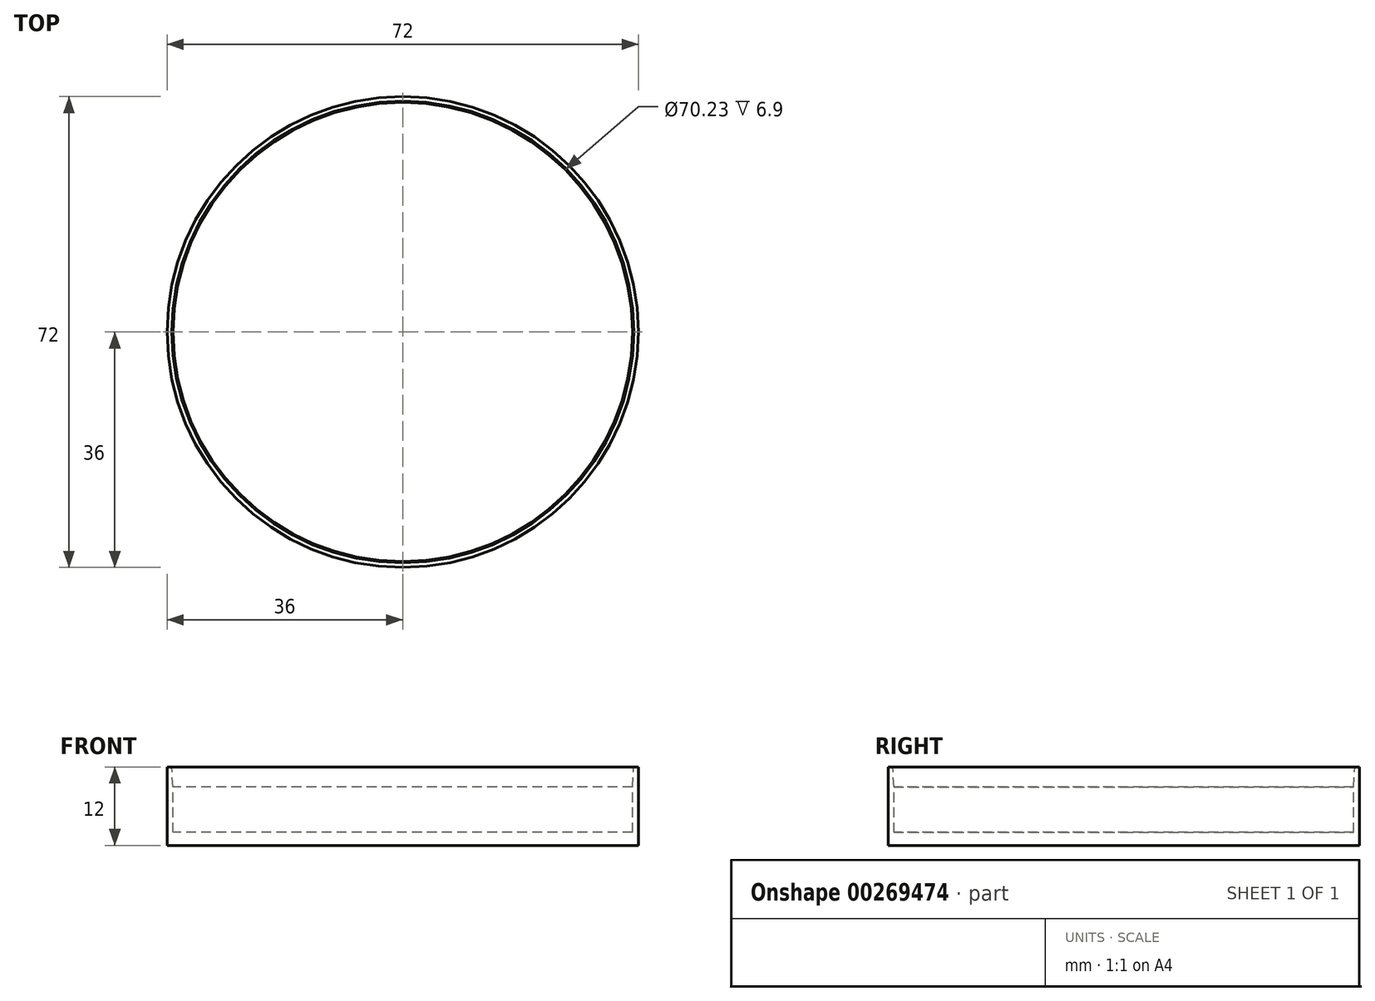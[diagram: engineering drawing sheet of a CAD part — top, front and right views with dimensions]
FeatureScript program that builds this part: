
annotation { "Feature Type Name" : "Feature", "Feature Type Description" : "" }
export const myFeature = defineFeature(function(context is Context, id is Id, definition is map)
    precondition{}
    {
        {
            var Q0;
            Q0=qCreatedBy(makeId("Top.planeOp"),FACE);
            var sketch = newSketch(context, id + "F0", { "sketchPlane" : qUnion([Q0])});
            skCircle(sketch, "E0", {"center": v(0, 0) * mm, "radius": 36 * mm});
            skSolve(sketch);
        }
        {
            var Q0;
            Q0=makeQuery(id+"F0.imprint","IMPRINT",FACE,{"disambiguationData":[TD([[makeQuery(id+"F0.imprint","IMPRINT",EDGE,{"derivedFrom":sQuery(id+"F0.wireOp",EDGE,"E0")}),1.0]])]});
            var Q1;
            Q1 = qSketchRegion(id + "F0", true);
            extrude(context, id + "F1", {"entities" : qUnion([Q0, Q1]), "depth" : 12 * mm});
        }
        {
            var Q0;
            Q0=makeQuery(id+"F1.opExtrude","CAP_FACE",FACE,{"disambiguationData":[OSD([sQuery(id+"F0.wireOp",EDGE,"E0")])],"isStart":false});
            var sketch = newSketch(context, id + "F2", { "sketchPlane" : qUnion([Q0])});
            skCircle(sketch, "E1", {"center": v(0, 0) * mm, "radius": 35 * mm});
            skSolve(sketch);
        }
        {
            var Q0;
            Q0=qCreatedBy(makeId("Front.planeOp"),FACE);
            var sketch = newSketch(context, id + "F3", { "sketchPlane" : qUnion([Q0])});
            skPoint(sketch, "E2", {"position": v(0, 12) * mm});
            skPoint(sketch, "E3", {"position": v(0, 2) * mm});
            skPoint(sketch, "E4", {"position": v(-35.11, 2) * mm});
            skPoint(sketch, "E5", {"position": v(-35.3, 12) * mm});
            skLineSegment(sketch, "E6", {"start": v(-35.11, 2) * mm, "end": v(0, 2) * mm});
            skLineSegment(sketch, "E7", {"start": v(0, 2) * mm, "end": v(0, 12) * mm});
            skLineSegment(sketch, "E8", {"start": v(-35.3, 12) * mm, "end": v(0, 12) * mm});
            skPoint(sketch, "E9", {"position": v(0, 7) * mm});
            skPoint(sketch, "E10", {"position": v(-35.11, 8.9) * mm});
            skPoint(sketch, "E11", {"position": v(-19.98, 7) * mm});
            skLineSegment(sketch, "E12", {"start": v(-35.3, 12) * mm, "end": v(-35.11, 8.9) * mm});
            skLineSegment(sketch, "E13", {"start": v(-35.11, 8.9) * mm, "end": v(-35.3, 12) * mm});
            skLineSegment(sketch, "E14", {"start": v(-35.11, 8.9) * mm, "end": v(-35.11, 2) * mm});
            skSolve(sketch);
        }
        {
            var Q0;
            Q0 = qSketchRegion(id + "F3", true);
            var Q1;
            Q1=sQuery(id+"F3.wireOp",EDGE,"E7");
            revolve(context, id + "F4", {"operationType" : NewBodyOperationType.REMOVE, "entities" : qUnion([Q0]), "axis" : qUnion([Q1]), "revolveType" : RevolveType.FULL, "oppositeDirection" : true});
        }
    });
